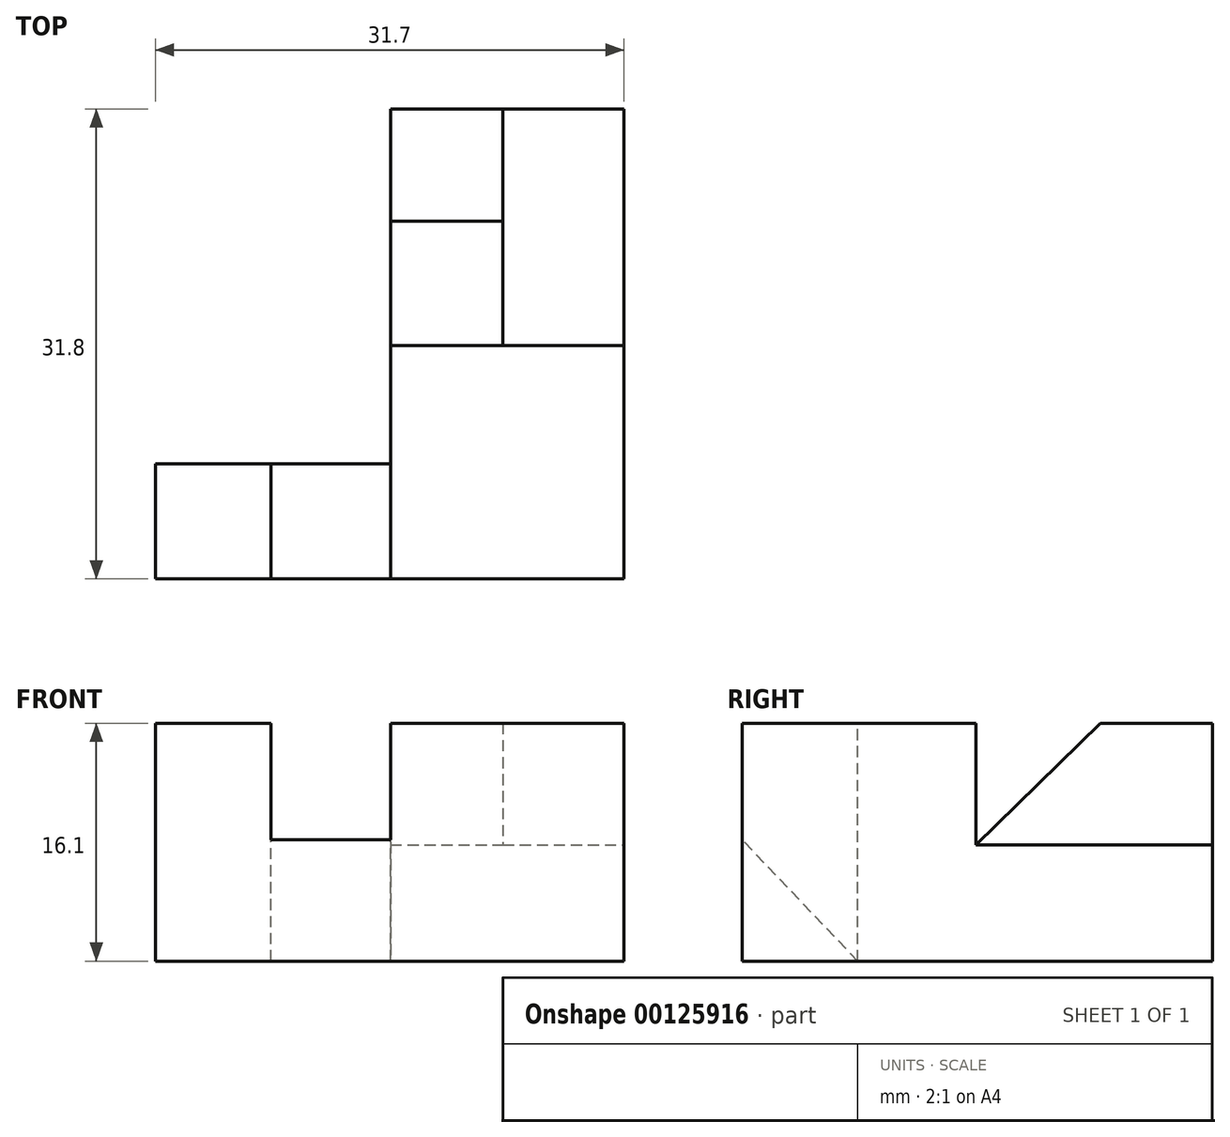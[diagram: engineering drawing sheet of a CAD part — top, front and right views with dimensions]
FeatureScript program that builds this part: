
annotation { "Feature Type Name" : "Feature", "Feature Type Description" : "" }
export const myFeature = defineFeature(function(context is Context, id is Id, definition is map)
    precondition{}
    {
        {
            var Q0;
            Q0=qCreatedBy(makeId("Top.planeOp"),FACE);
            var sketch = newSketch(context, id + "F0", { "sketchPlane" : qUnion([Q0])});
            skLineSegment(sketch, "E0.bottom", {"start": v(-8.6, -9.09) * mm, "end": v(7.2, -9.09) * mm});
            skLineSegment(sketch, "E0.top", {"start": v(-8.6, 6.71) * mm, "end": v(7.2, 6.71) * mm});
            skLineSegment(sketch, "E0.left", {"start": v(-8.6, -9.09) * mm, "end": v(-8.6, 6.71) * mm});
            skLineSegment(sketch, "E0.right", {"start": v(7.2, -9.09) * mm, "end": v(7.2, 6.71) * mm});
            skSolve(sketch);
        }
        {
            var Q0;
            Q0=makeQuery(id+"F0.imprint","IMPRINT",FACE,{"disambiguationData":[TD([[makeQuery(id+"F0.imprint","IMPRINT",EDGE,{"derivedFrom":sQuery(id+"F0.wireOp",EDGE,"E0.bottom")}),1.0]])]});
            extrude(context, id + "F1", {"entities" : qUnion([Q0]), "depth" : 16.1 * mm});
        }
        {
            var Q0;
            Q0=makeQuery(id+"F1.opExtrude","SWEPT_FACE",FACE,{"disambiguationData":[OSD([sQuery(id+"F0.wireOp",EDGE,"E0.left")])]});
            var sketch = newSketch(context, id + "F2", { "sketchPlane" : qUnion([Q0])});
            skLineSegment(sketch, "E1", {"start": v(9.09, 0) * mm, "end": v(9.09, 8.2) * mm});
            skLineSegment(sketch, "E2", {"start": v(9.09, 0) * mm, "end": v(1.29, 0) * mm});
            skLineSegment(sketch, "E3", {"start": v(1.29, 0) * mm, "end": v(9.09, 8.2) * mm});
            skSolve(sketch);
        }
        {
            var Q0;
            Q0=makeQuery(id+"F2.imprint","IMPRINT",FACE,{"disambiguationData":[TD([[makeQuery(id+"F2.imprint","IMPRINT",EDGE,{"derivedFrom":sQuery(id+"F2.wireOp",EDGE,"E1")}),-1.0]])]});
            extrude(context, id + "F3", {"entities" : qUnion([Q0]), "operationType" : NewBodyOperationType.ADD, "depth" : 8.1 * mm});
        }
        {
            var Q0;
            Q0=makeQuery(id+"F3.opExtrude","CAP_FACE",FACE,{"disambiguationData":[OSD([sQuery(id+"F2.wireOp",EDGE,"E1"),sQuery(id+"F2.wireOp",EDGE,"E2"),sQuery(id+"F2.wireOp",EDGE,"E3")])],"isStart":false});
            var sketch = newSketch(context, id + "F4", { "sketchPlane" : qUnion([Q0])});
            skLineSegment(sketch, "E4.bottom", {"start": v(9.09, 0) * mm, "end": v(1.29, 0) * mm});
            skLineSegment(sketch, "E4.top", {"start": v(9.09, 16.1) * mm, "end": v(1.29, 16.1) * mm});
            skLineSegment(sketch, "E4.left", {"start": v(9.09, 0) * mm, "end": v(9.09, 16.1) * mm});
            skLineSegment(sketch, "E4.right", {"start": v(1.29, 0) * mm, "end": v(1.29, 16.1) * mm});
            skSolve(sketch);
        }
        {
            var Q0;
            {var subQ0=sQuery(id+"F4.wireOp",EDGE,"E4.top");Q0=makeQuery(id+"F4.imprint","IMPRINT",FACE,{"disambiguationData":[TD([[makeQuery(id+"F4.imprint","IMPRINT",EDGE,{"derivedFrom":subQ0}),1.0]])]});}
            var Q1;
            {var subQ0=sQuery(id+"F4.wireOp",EDGE,"E4.bottom");Q1=makeQuery(id+"F4.imprint","IMPRINT",FACE,{"disambiguationData":[TD([[makeQuery(id+"F4.imprint","IMPRINT",EDGE,{"derivedFrom":subQ0}),-1.0]])]});}
            extrude(context, id + "F5", {"entities" : qUnion([Q0, Q1]), "operationType" : NewBodyOperationType.ADD, "depth" : 7.8 * mm});
        }
        {
            var Q0;
            Q0=makeQuery(id+"F5.boolean.opBoolean","MERGE",FACE,{"derivedFrom":[makeQuery(id+"F3.boolean.opBoolean","MERGE",FACE,{"derivedFrom":[makeQuery(id+"F1.opExtrude","CAP_FACE",FACE,{"disambiguationData":[OSD([sQuery(id+"F0.wireOp",EDGE,"E0.bottom"),sQuery(id+"F0.wireOp",EDGE,"E0.top"),sQuery(id+"F0.wireOp",EDGE,"E0.left"),sQuery(id+"F0.wireOp",EDGE,"E0.right")])],"isStart":true}),makeQuery(id+"F3.opExtrude","SWEPT_FACE",FACE,{"disambiguationData":[OSD([sQuery(id+"F2.wireOp",EDGE,"E2")])]})]}),makeQuery(id+"F5.opExtrude","SWEPT_FACE",FACE,{"disambiguationData":[OSD([sQuery(id+"F4.wireOp",EDGE,"E4.bottom")])]})]});
            var sketch = newSketch(context, id + "F6", { "sketchPlane" : qUnion([Q0])});
            skLineSegment(sketch, "E5.bottom", {"start": v(7.2, -6.71) * mm, "end": v(-8.6, -6.71) * mm});
            skLineSegment(sketch, "E5.top", {"start": v(7.2, -22.71) * mm, "end": v(-8.6, -22.71) * mm});
            skLineSegment(sketch, "E5.left", {"start": v(7.2, -6.71) * mm, "end": v(7.2, -22.71) * mm});
            skLineSegment(sketch, "E5.right", {"start": v(-8.6, -6.71) * mm, "end": v(-8.6, -22.71) * mm});
            skSolve(sketch);
        }
        {
            var Q0;
            Q0=makeQuery(id+"F6.imprint","IMPRINT",FACE,{"disambiguationData":[TD([[makeQuery(id+"F6.imprint","IMPRINT",EDGE,{"derivedFrom":sQuery(id+"F6.wireOp",EDGE,"E5.bottom")}),-1.0]])]});
            extrude(context, id + "F7", {"entities" : qUnion([Q0]), "operationType" : NewBodyOperationType.ADD, "oppositeDirection" : true, "depth" : 7.85 * mm});
        }
        {
            var Q0;
            Q0=makeQuery(id+"F7.opExtrude","CAP_FACE",FACE,{"disambiguationData":[OSD([sQuery(id+"F6.wireOp",EDGE,"E5.bottom"),sQuery(id+"F6.wireOp",EDGE,"E5.top"),sQuery(id+"F6.wireOp",EDGE,"E5.left"),sQuery(id+"F6.wireOp",EDGE,"E5.right")])],"isStart":false});
            var sketch = newSketch(context, id + "F8", { "sketchPlane" : qUnion([Q0])});
            skLineSegment(sketch, "E6.bottom", {"start": v(-8.6, 22.71) * mm, "end": v(-1, 22.71) * mm});
            skLineSegment(sketch, "E6.top", {"start": v(-8.6, 15.11) * mm, "end": v(-1, 15.11) * mm});
            skLineSegment(sketch, "E6.left", {"start": v(-8.6, 22.71) * mm, "end": v(-8.6, 15.11) * mm});
            skLineSegment(sketch, "E6.right", {"start": v(-1, 22.71) * mm, "end": v(-1, 15.11) * mm});
            skSolve(sketch);
        }
        {
            var Q0;
            Q0=makeQuery(id+"F8.imprint","IMPRINT",FACE,{"disambiguationData":[TD([[makeQuery(id+"F8.imprint","IMPRINT",EDGE,{"derivedFrom":sQuery(id+"F8.wireOp",EDGE,"E6.bottom")}),1.0]])]});
            var Q1;
            Q1=makeQuery(id+"F1.opExtrude","CAP_FACE",FACE,{"disambiguationData":[OSD([sQuery(id+"F0.wireOp",EDGE,"E0.bottom"),sQuery(id+"F0.wireOp",EDGE,"E0.top"),sQuery(id+"F0.wireOp",EDGE,"E0.left"),sQuery(id+"F0.wireOp",EDGE,"E0.right")])],"isStart":false});
            extrude(context, id + "F9", {"entities" : qUnion([Q0]), "operationType" : NewBodyOperationType.ADD, "endBound" : BoundingType.UP_TO_SURFACE, "endBoundEntityFace" : qUnion([Q1]), "depth" : 25.4 * mm});
        }
        {
            var Q0;
            Q0=makeQuery(id+"F9.boolean.opBoolean","MERGE",FACE,{"derivedFrom":[makeQuery(id+"F7.opExtrude","SWEPT_FACE",FACE,{"disambiguationData":[OSD([sQuery(id+"F6.wireOp",EDGE,"E5.right")])]}),makeQuery(id+"F9.opExtrude","SWEPT_FACE",FACE,{"disambiguationData":[OSD([sQuery(id+"F8.wireOp",EDGE,"E6.left")])]})]});
            var sketch = newSketch(context, id + "F10", { "sketchPlane" : qUnion([Q0])});
            skLineSegment(sketch, "E7", {"start": v(-15.11, 16.1) * mm, "end": v(-6.71, 7.85) * mm});
            skSolve(sketch);
        }
        {
            var Q0;
            Q0=makeQuery(id+"F10.imprint","IMPRINT",FACE,{"disambiguationData":[TD([[makeQuery(id+"F10.imprint","IMPRINT",EDGE,{"derivedFrom":sQuery(id+"F10.wireOp",EDGE,"E7")}),-1.0]])]});
            var Q1;
            Q1=makeQuery(id+"F9.opExtrude","SWEPT_FACE",FACE,{"disambiguationData":[OSD([sQuery(id+"F8.wireOp",EDGE,"E6.right")])]});
            extrude(context, id + "F11", {"entities" : qUnion([Q0]), "operationType" : NewBodyOperationType.ADD, "endBound" : BoundingType.UP_TO_SURFACE, "oppositeDirection" : true, "endBoundEntityFace" : qUnion([Q1]), "depth" : 25.4 * mm});
        }
    });
